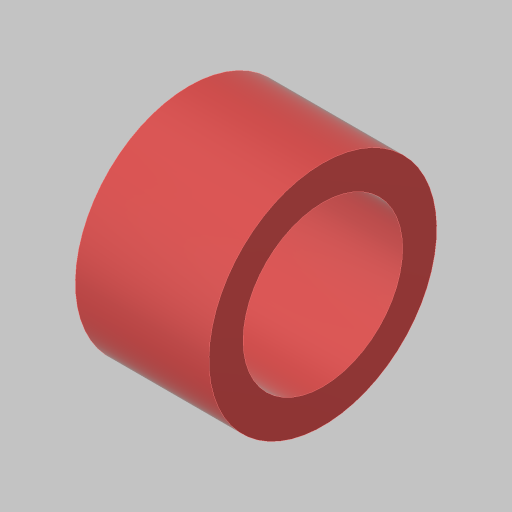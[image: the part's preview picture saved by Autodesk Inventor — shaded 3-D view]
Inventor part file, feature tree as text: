
AUTODESK INVENTOR PART (.ipt)
format: ipt  version: 2023.5 (Build 275446000, 446)  size: 113,664 bytes
history: native  units: in
note: dims shown in document units (in); Inventor stores cm internally (conversion verified against a paired STEP export)
features: extrude x1, sketch x1
ambient origin geometry x8: Origin, YZ Plane, XZ Plane, XY Plane, X Axis, Y Axis, Z Axis, Center Point
bodies: Solid1 (feature_tree)
feature tree (2):
  extrude  "Extrusion1"  Depth=0.49in
  sketch  "Sketch1"  dims[d0=0.585in d1=0.125in d2=0.49in d3=0.0in]
